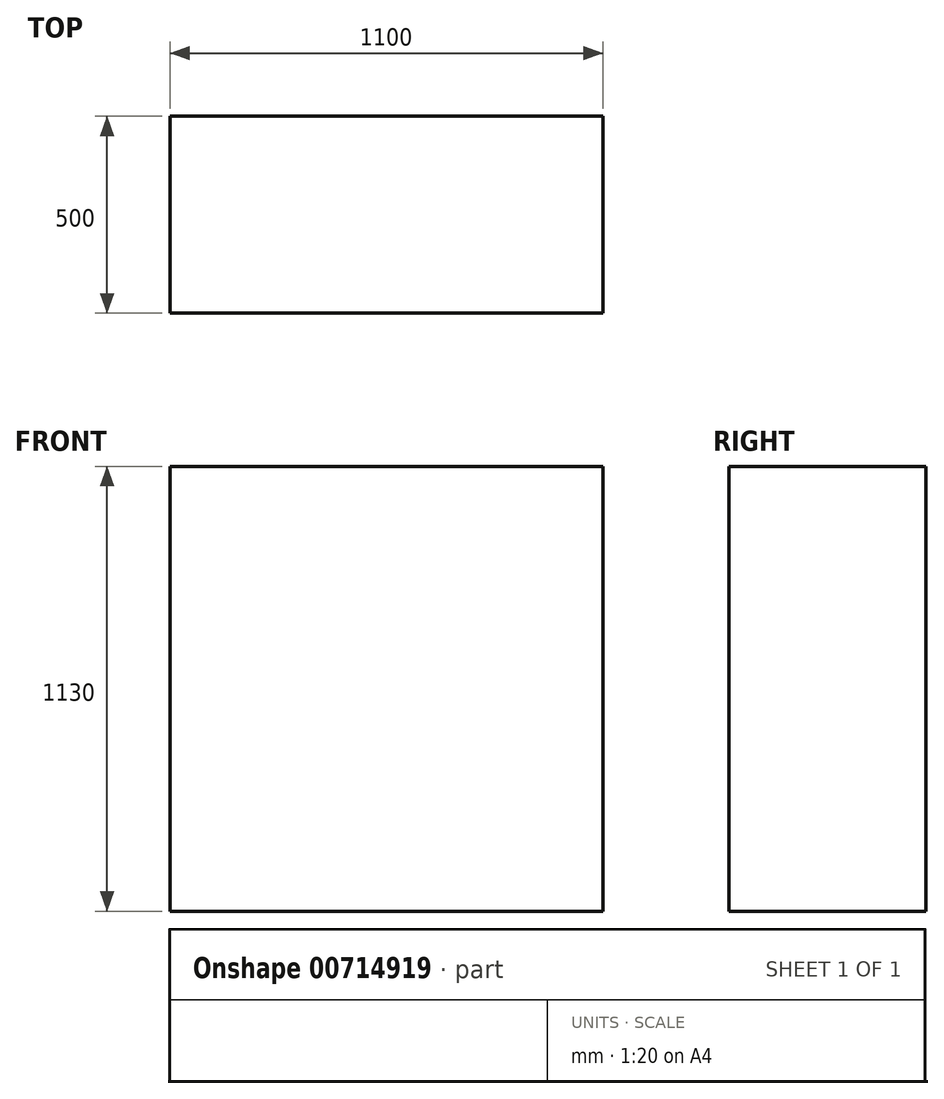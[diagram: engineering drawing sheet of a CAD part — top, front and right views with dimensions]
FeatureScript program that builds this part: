
annotation { "Feature Type Name" : "Feature", "Feature Type Description" : "" }
export const myFeature = defineFeature(function(context is Context, id is Id, definition is map)
    precondition{}
    {
        {
            var Q0;
            Q0=qCreatedBy(makeId("Top.planeOp"),FACE);
            var sketch = newSketch(context, id + "F0", { "sketchPlane" : qUnion([Q0])});
            skLineSegment(sketch, "E0.bottom", {"start": v(0, 0) * mm, "end": v(1100, 0) * mm});
            skLineSegment(sketch, "E0.top", {"start": v(0, -500) * mm, "end": v(1100, -500) * mm});
            skLineSegment(sketch, "E0.left", {"start": v(0, 0) * mm, "end": v(0, -500) * mm});
            skLineSegment(sketch, "E0.right", {"start": v(1100, 0) * mm, "end": v(1100, -500) * mm});
            skSolve(sketch);
        }
        {
            var Q0;
            Q0 = qSketchRegion(id + "F0", true);
            extrude(context, id + "F1", {"entities" : qUnion([Q0]), "depth" : 1130 * mm, "offsetDistance" : 25 * mm});
        }
    });
